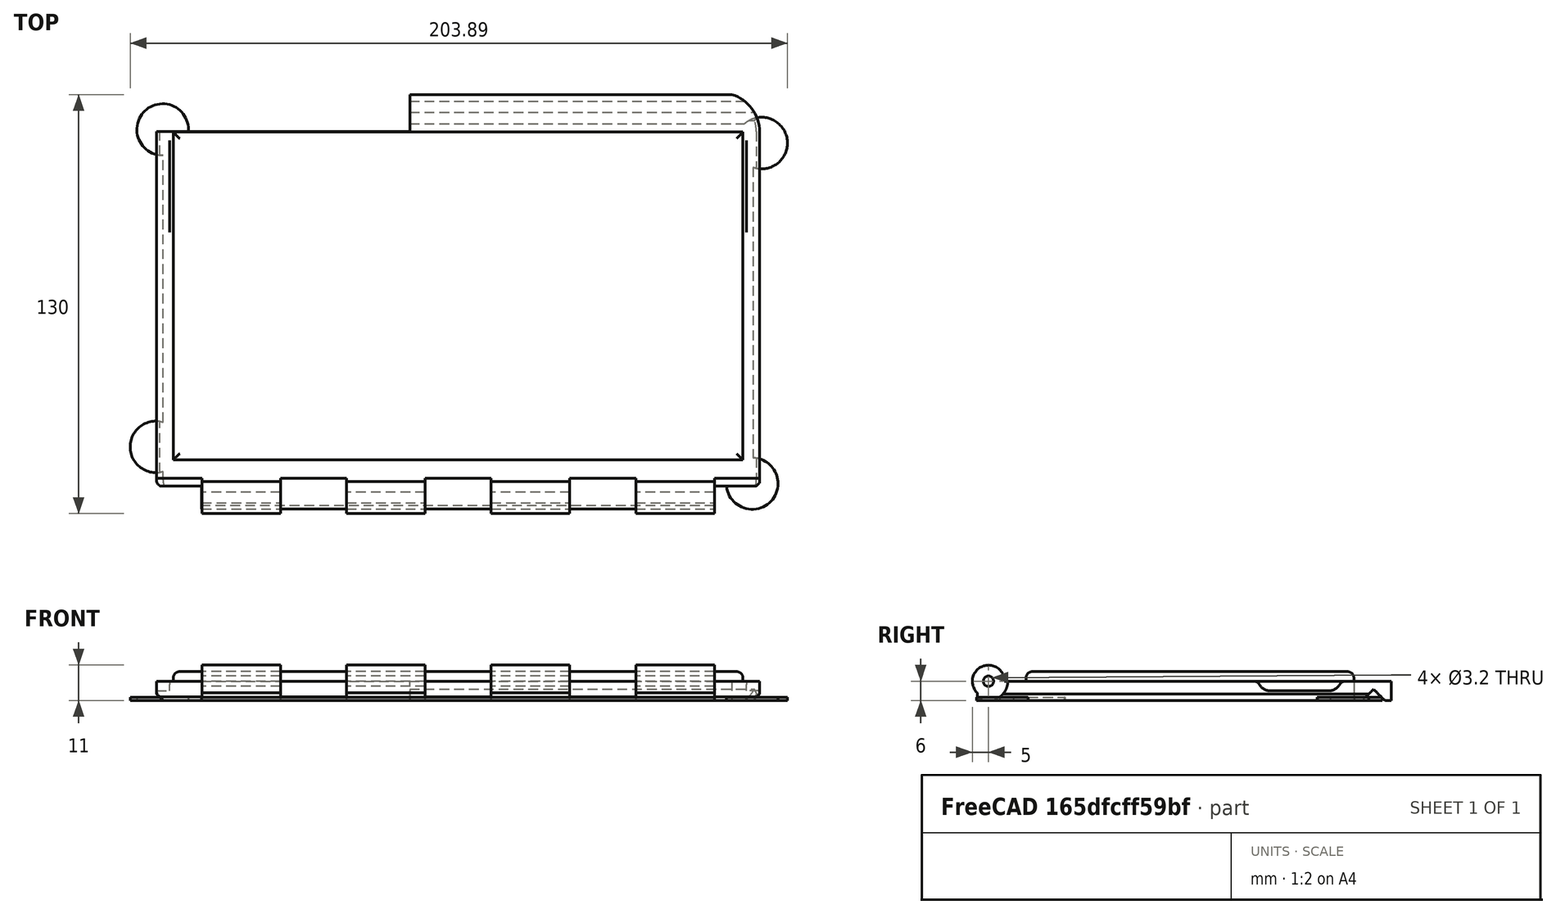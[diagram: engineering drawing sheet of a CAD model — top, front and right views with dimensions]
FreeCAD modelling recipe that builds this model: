
FCSTD DOCUMENT  (FreeCAD 0.19R)
Label: SwitchCaseSmallRLidLatch6mm
License: All rights reserved
LicenseURL: http://en.wikipedia.org/wiki/All_rights_reserved
objects: Sketcher::SketchObject×13, PartDesign::Pocket×8, PartDesign::Pad×4, PartDesign::Chamfer×3, PartDesign::Fillet×2, Mesh::Feature×1, PartDesign::Body×1, PartDesign::LinearPattern×1
note: 49 computed .brp shape members not serialized (recipe doc carries the construction recipe); baked Part::Feature solids carry a one-line shape summary decoded from their .brp

FEATURE [Sketcher::SketchObject] Sketch
  FullyConstrained = false
  MapMode = 5
  Support = -> [XY_Plane]
  sketch-geometry (4):
    g0: LineSegment StartX=-100 StartY=62.5 StartZ=0 EndX=100 EndY=62.5 EndZ=0
    g1: LineSegment StartX=100 StartY=62.5 StartZ=0 EndX=100 EndY=-66 EndZ=0
    g2: LineSegment StartX=100 StartY=-66 StartZ=0 EndX=-100 EndY=-66 EndZ=0
    g3: LineSegment StartX=-100 StartY=-66 StartZ=0 EndX=-100 EndY=62.5 EndZ=0
  constraints (11):
    c: Coincident(g0,g1)
    c: Coincident(g1,g2)
    c: Coincident(g2,g3)
    c: Coincident(g3,g0)
    c: Horizontal(g0)
    c: Horizontal(g2)
    c: Vertical(g1)
    c: Vertical(g3)
    c: Distance(g0) = 200
    c: DistanceY(g2) = -66
    c: DistanceY(g0) = 62.5
FEATURE [PartDesign::Pad] Pad
  Direction = (1,1,1)
  Length = 6
  Length2 = 100
  Profile = -> Sketch
  Type = 0
FEATURE [Sketcher::SketchObject] Sketch001
  FullyConstrained = true
  MapMode = 5
  Placement = pos=(0,0,6) rot=(0,0,1;0rad)
  Support = -> [Pad]
  sketch-geometry (4):
    g0: LineSegment StartX=-88.375 StartY=50.875 StartZ=0 EndX=88.375 EndY=50.875 EndZ=0
    g1: LineSegment StartX=88.375 StartY=50.875 StartZ=0 EndX=88.375 EndY=-50.875 EndZ=0
    g2: LineSegment StartX=88.375 StartY=-50.875 StartZ=0 EndX=-88.375 EndY=-50.875 EndZ=0
    g3: LineSegment StartX=-88.375 StartY=-50.875 StartZ=0 EndX=-88.375 EndY=50.875 EndZ=0
  constraints (11):
    c: Coincident(g0,g1)
    c: Coincident(g1,g2)
    c: Coincident(g2,g3)
    c: Coincident(g3,g0)
    c: Horizontal(g0)
    c: Horizontal(g2)
    c: Vertical(g1)
    c: Vertical(g3)
    c: Distance(g0) = 176.75
    c: Distance(g1) = 101.75
    c: Symmetric(g0,g2,g-1)
FEATURE [PartDesign::Pad] Pad001
  BaseFeature = -> Pad
  Direction = (1,1,1)
  Length = 3
  Length2 = 100
  Profile = -> Sketch001
  Type = 0
FEATURE [Sketcher::SketchObject] Sketch003
  ExternalGeometry = -> [Pad001]
  FullyConstrained = true
  MapMode = 5
  Placement = pos=(0,0,0) rot=(1,0,0;3.14159rad)
  Support = -> [Pad001]
  sketch-geometry (4):
    g0: LineSegment StartX=-15 StartY=-62.5 StartZ=0 EndX=-100 EndY=-62.5 EndZ=0
    g1: LineSegment StartX=-100 StartY=-62.5 StartZ=0 EndX=-100 EndY=-51 EndZ=0
    g2: LineSegment StartX=-100 StartY=-51 StartZ=0 EndX=-15 EndY=-51 EndZ=0
    g3: LineSegment StartX=-15 StartY=-51 StartZ=0 EndX=-15 EndY=-62.5 EndZ=0
  constraints (11):
    c: Coincident(g0,g1)
    c: Coincident(g1,g2)
    c: Coincident(g2,g3)
    c: Coincident(g3,g0)
    c: Horizontal(g0)
    c: Horizontal(g2)
    c: Vertical(g1)
    c: Vertical(g3)
    c: Distance(g1) = 11.5
    c: DistanceX(g0) = -15
    c: Coincident(g0,g-3)
FEATURE [PartDesign::Pocket] Pocket
  BaseFeature = -> Pad001
  Length = 5
  Length2 = 100
  Profile = -> Sketch003
  Type = 1
FEATURE [Sketcher::SketchObject] Sketch005
  FullyConstrained = true
  MapMode = 5
  Placement = pos=(100,0,0) rot=(0.57735,0.57735,0.57735;2.0944rad)
  Support = -> [Pocket]
FEATURE [Sketcher::SketchObject] Sketch006
  ExternalGeometry = -> [Pocket]
  FullyConstrained = true
  MapMode = 5
  Placement = pos=(-15,0,0) rot=(0.57735,-0.57735,-0.57735;2.0944rad)
  Support = -> [Pocket]
  sketch-geometry (4):
    g0: LineSegment StartX=-56.9645 StartY=3.53553 StartZ=0 EndX=-60.5 EndY=0 EndZ=0
    g1: LineSegment StartX=-60.5 StartY=0 StartZ=0 EndX=-56.9645 EndY=-3.53553 EndZ=0
    g2: LineSegment StartX=-56.9645 StartY=-3.53553 StartZ=0 EndX=-53.4289 EndY=0 EndZ=0
    g3: LineSegment StartX=-53.4289 StartY=0 StartZ=0 EndX=-56.9645 EndY=3.53553 EndZ=0
  constraints (12):
    c: Coincident(g0,g1)
    c: Coincident(g1,g2)
    c: Coincident(g2,g3)
    c: Coincident(g3,g0)
    c: Perpendicular(g0,g3)
    c: Perpendicular(g0,g1)
    c: Equal(g3,g0)
    c: Equal(g0,g1)
    c: Distance(g3) = 5
    c: PointOnObject(g0,g-4)
    c: PointOnObject(g2,g-4)
    c: Distance(g0,g-4) = 2
FEATURE [PartDesign::Pocket] Pocket001  label="pocket_dovetail"
  BaseFeature = -> Pocket
  Length = 5
  Length2 = 100
  Profile = -> Sketch006
  Type = 1
FEATURE [Sketcher::SketchObject] Sketch012
  FullyConstrained = true
  MapMode = 5
  Placement = pos=(-93.5,-1.2e-14,0) rot=(0.57735,-0.57735,-0.57735;2.0944rad)
  sketch-geometry (4):
    g0: ArcOfCircle CenterX=-43 CenterY=7 CenterZ=0 NormalX=0 NormalY=0 NormalZ=1 AngleXU=0 Radius=4 StartAngle=1.5708 EndAngle=4.71239
    g1: ArcOfCircle CenterX=-25 CenterY=7 CenterZ=0 NormalX=0 NormalY=0 NormalZ=1 AngleXU=0 Radius=4 StartAngle=4.71239 EndAngle=7.85398
    g2: LineSegment StartX=-43 StartY=3 StartZ=0 EndX=-25 EndY=3 EndZ=0
    g3: LineSegment StartX=-43 StartY=11 StartZ=0 EndX=-25 EndY=11 EndZ=0
  constraints (10):
    c: Tangent(g0,g3) = 1.5708
    c: Tangent(g0,g2) = -1.5708
    c: Tangent(g2,g1) = -1.5708
    c: Tangent(g3,g1) = 1.5708
    c: Horizontal(g2)
    c: Equal(g0,g1)
    c: Distance(g3) = 18
    c: Distance(g1,g1) = 8
    c: DistanceY(g1) = 3
    c: DistanceX(g1) = -25
FEATURE [Sketcher::SketchObject] Sketch013
  FullyConstrained = true
  MapMode = 5
  Placement = pos=(93.5,0,0) rot=(0.57735,0.57735,0.57735;2.0944rad)
  sketch-geometry (4):
    g0: ArcOfCircle CenterX=25 CenterY=7 CenterZ=0 NormalX=0 NormalY=0 NormalZ=1 AngleXU=0 Radius=4 StartAngle=1.5708 EndAngle=4.71239
    g1: ArcOfCircle CenterX=43 CenterY=7 CenterZ=0 NormalX=0 NormalY=0 NormalZ=1 AngleXU=0 Radius=4 StartAngle=4.71239 EndAngle=7.85398
    g2: LineSegment StartX=25 StartY=3 StartZ=0 EndX=43 EndY=3 EndZ=0
    g3: LineSegment StartX=25 StartY=11 StartZ=0 EndX=43 EndY=11 EndZ=0
  constraints (10):
    c: Tangent(g0,g3) = 1.5708
    c: Tangent(g0,g2) = -1.5708
    c: Tangent(g2,g1) = -1.5708
    c: Tangent(g3,g1) = 1.5708
    c: Horizontal(g2)
    c: Equal(g0,g1)
    c: Distance(g1,g1) = 8
    c: Distance(g3) = 18
    c: DistanceY(g0) = 3
    c: DistanceX(g0) = 25
FEATURE [Mesh::Feature] Mesh  label="Pad003 (Meshed)"
FEATURE [PartDesign::Body] Body
  Group = -> [Sketch,Pad,Sketch001,Pad001,Sketch003,Pocket,Sketch005,Sketch006,Pocket001,Sketch007,Sketch008,Pad002,Sketch009,Pocket002,LinearPattern,Sketch010,Pocket003,Chamfer,Sketch011,Pocket004,Pocket005,Chamfer001,Sketch012,Sketch013,Chamfer002,Pocket006,Pocket007,Fillet,Fillet001,Sketch014,Pad003]
  Origin = -> Origin
  Tip = -> Pad003
FEATURE [Sketcher::SketchObject] Sketch007
  FullyConstrained = true
  MapMode = 5
  Placement = pos=(0,0,0) rot=(1,0,0;3.14159rad)
  Support = -> [Pocket004]
  sketch-geometry (9):
    g0: LineSegment StartX=-93.5 StartY=57 StartZ=0 EndX=-93.5 EndY=-51 EndZ=0
    g1: LineSegment StartX=-81.5 StartY=-63 StartZ=0 EndX=81.5 EndY=-63 EndZ=0
    g2: LineSegment StartX=93.5 StartY=-51 StartZ=0 EndX=93.5 EndY=57 EndZ=0
    g3: LineSegment StartX=81.5 StartY=69 StartZ=0 EndX=-81.5 EndY=69 EndZ=0
    g4: ArcOfCircle CenterX=81.5 CenterY=57 CenterZ=0 NormalX=0 NormalY=0 NormalZ=1 AngleXU=0 Radius=12 StartAngle=0 EndAngle=1.5708
    g5: ArcOfCircle CenterX=-81.5 CenterY=57 CenterZ=0 NormalX=0 NormalY=0 NormalZ=1 AngleXU=0 Radius=12 StartAngle=1.5708 EndAngle=3.14159
    g6: ArcOfCircle CenterX=-81.5 CenterY=-51 CenterZ=0 NormalX=0 NormalY=0 NormalZ=1 AngleXU=0 Radius=12 StartAngle=3.14159 EndAngle=4.71239
    g7: ArcOfCircle CenterX=81.5 CenterY=-51 CenterZ=0 NormalX=0 NormalY=0 NormalZ=1 AngleXU=0 Radius=12 StartAngle=4.71239 EndAngle=6.28319
    g8: Circle CenterX=0 CenterY=0 CenterZ=0 NormalX=0 NormalY=0 NormalZ=1 AngleXU=0 Radius=191.08
  constraints (21):
    c: Equal(g2,g0)
    c: Horizontal(g3)
    c: Vertical(g2)
    c: Equal(g1,g3)
    c: Tangent(g3,g4) = -1.5708
    c: Tangent(g2,g4) = -1.5708
    c: Tangent(g3,g5) = -1.5708
    c: Tangent(g0,g5) = -1.5708
    c: Tangent(g0,g6) = -1.5708
    c: Tangent(g1,g6) = -1.5708
    c: Tangent(g1,g7) = -1.5708
    c: Tangent(g2,g7) = -1.5708
    c: Radius(g4) = 12
    c: Equal(g4,g5)
    c: Equal(g4,g6)
    c: Symmetric(g2,g0,g-2)
    c: DistanceY(g3) = 69
    c: DistanceY(g1) = -63
    c: Distance(g2,g0) = 187
    c: Coincident(g8,g-1)
    c: Radius(g8) = 191.08
FEATURE [Sketcher::SketchObject] Sketch008
  ExternalGeometry = -> [Sketch007,Pocket001]
  FullyConstrained = true
  MapMode = 5
  Placement = pos=(100,0,0) rot=(0.57735,0.57735,0.57735;2.0944rad)
  Support = -> [Pocket001]
  sketch-geometry (1):
    g0: Circle CenterX=-62.5 CenterY=6 CenterZ=0 NormalX=0 NormalY=0 NormalZ=1 AngleXU=0 Radius=5
  constraints (3):
    c: Radius(g0) = 5
    c: PointOnObject(g0,g-4)
    c: DistanceX(g0) = -62.5
FEATURE [PartDesign::Pad] Pad002
  BaseFeature = -> Pocket001
  Direction = (1,1,1)
  Length = 200
  Length2 = 100
  Profile = -> Sketch008
  Reversed = true
  Type = 0
FEATURE [Sketcher::SketchObject] Sketch009
  ExternalGeometry = -> [Pad002]
  FullyConstrained = true
  MapMode = 5
  Placement = pos=(100,0,0) rot=(0.57735,0.57735,0.57735;2.0944rad)
  Support = -> [Pad002]
  sketch-geometry (1):
    g0: Circle CenterX=-62.5 CenterY=6 CenterZ=0 NormalX=0 NormalY=0 NormalZ=1 AngleXU=0 Radius=6
  constraints (3):
    c: Radius(g0) = 6
    c: PointOnObject(g0,g-6)
    c: DistanceX(g0) = -62.5
FEATURE [PartDesign::Pocket] Pocket002  label="hingepocket"
  BaseFeature = -> Pad002
  Length = 20.5
  Length2 = 100
  Profile = -> Sketch009
  Type = 0
FEATURE [PartDesign::LinearPattern] LinearPattern
  BaseFeature = -> Pocket002
  Direction = -> X_Axis
  Length = 179.5
  Occurrences = 5
  Originals = -> [Pocket002]
  Reversed = true
FEATURE [Sketcher::SketchObject] Sketch010
  ExternalGeometry = -> [LinearPattern]
  FullyConstrained = true
  MapMode = 5
  Placement = pos=(-79.5,0,0) rot=(0.57735,-0.57735,-0.57735;2.0944rad)
  Support = -> [LinearPattern]
  sketch-geometry (1):
    g0: Circle CenterX=62.5 CenterY=6 CenterZ=0 NormalX=0 NormalY=0 NormalZ=1 AngleXU=0 Radius=1.6
  constraints (3):
    c: Radius(g0) = 1.6
    c: DistanceX(g0) = 62.5
    c: DistanceY(g0) = 6
FEATURE [PartDesign::Pocket] Pocket003  label="hingepin"
  BaseFeature = -> LinearPattern
  Length = 5
  Length2 = 100
  Profile = -> Sketch010
  Type = 1
FEATURE [PartDesign::Chamfer] Chamfer
  Angle = 45
  Base = -> Pocket003 [Edge46]
  BaseFeature = -> Pocket003
  ChamferType = 0
  FlipDirection = false
  Size = 1
  Size2 = 1
  SupportTransform = false
FEATURE [Sketcher::SketchObject] Sketch011
  FullyConstrained = false
  MapMode = 5
  Placement = pos=(0,0,0) rot=(1,0,0;3.14159rad)
  Support = -> [Chamfer]
  sketch-geometry (8):
    g0: LineSegment StartX=-103.879 StartY=59 StartZ=0 EndX=-79.55 EndY=59 EndZ=0
    g1: LineSegment StartX=-79.55 StartY=59 StartZ=0 EndX=-79.55 EndY=72.9041 EndZ=0
    g2: LineSegment StartX=-79.55 StartY=72.9041 StartZ=0 EndX=-103.879 EndY=72.9041 EndZ=0
    g3: LineSegment StartX=-103.879 StartY=72.9041 StartZ=0 EndX=-103.879 EndY=59 EndZ=0
    g4: LineSegment StartX=79.55 StartY=72.9041 StartZ=0 EndX=107.401 EndY=72.9041 EndZ=0
    g5: LineSegment StartX=107.401 StartY=72.9041 StartZ=0 EndX=107.401 EndY=59 EndZ=0
    g6: LineSegment StartX=107.401 StartY=59 StartZ=0 EndX=79.55 EndY=59 EndZ=0
    g7: LineSegment StartX=79.55 StartY=59 StartZ=0 EndX=79.55 EndY=72.9041 EndZ=0
  constraints (20):
    c: Coincident(g0,g1)
    c: Coincident(g1,g2)
    c: Coincident(g2,g3)
    c: Coincident(g3,g0)
    c: Horizontal(g0)
    c: Horizontal(g2)
    c: Vertical(g1)
    c: Vertical(g3)
    c: Coincident(g4,g5)
    c: Coincident(g5,g6)
    c: Coincident(g6,g7)
    c: Coincident(g7,g4)
    c: Horizontal(g4)
    c: Horizontal(g6)
    c: Vertical(g5)
    c: Vertical(g7)
    c: DistanceY(g6) = 59
    c: DistanceY(g0) = 59
    c: Symmetric(g1,g4,g-2)
    c: Distance(g1,g4) = 159.1
FEATURE [PartDesign::Pocket] Pocket004
  BaseFeature = -> Chamfer
  Length = 5
  Length2 = 100
  Profile = -> Sketch011
  Type = 0
FEATURE [PartDesign::Pocket] Pocket005
  BaseFeature = -> Pocket004
  Length = 5
  Length2 = 100
  Profile = -> Sketch007
  Type = 1
FEATURE [PartDesign::Chamfer] Chamfer001
  Angle = 45
  Base = -> Pocket005 [Edge5]
  BaseFeature = -> Pocket005
  ChamferType = 0
  FlipDirection = false
  Size = 2
  Size2 = 1
  SupportTransform = false
FEATURE [PartDesign::Chamfer] Chamfer002
  Angle = 45
  Base = -> Chamfer001 [Edge14]
  BaseFeature = -> Chamfer001
  ChamferType = 0
  FlipDirection = false
  Size = 2
  Size2 = 1
  SupportTransform = false
FEATURE [PartDesign::Pocket] Pocket006
  BaseFeature = -> Chamfer002
  Length = 4
  Length2 = 100
  Profile = -> Sketch013
  Type = 0
FEATURE [PartDesign::Pocket] Pocket007
  BaseFeature = -> Pocket006
  Length = 4
  Length2 = 100
  Profile = -> Sketch012
  Type = 0
FEATURE [PartDesign::Fillet] Fillet
  Base = -> Pocket007 [Edge78,Edge76,Edge70,Edge72]
  BaseFeature = -> Pocket007
  Radius = 2
  SupportTransform = false
FEATURE [PartDesign::Fillet] Fillet001
  Base = -> Fillet [Face66]
  BaseFeature = -> Fillet
  Radius = 2
  SupportTransform = false
FEATURE [Sketcher::SketchObject] Sketch014
  FullyConstrained = false
  MapMode = 5
  Placement = pos=(0,0,0) rot=(1,0,0;3.14159rad)
  Support = -> [Fillet001]
  sketch-geometry (4):
    g0: Circle CenterX=-93.7329 CenterY=46.7924 CenterZ=0 NormalX=0 NormalY=0 NormalZ=1 AngleXU=0 Radius=8
    g1: Circle CenterX=91.242 CenterY=58.1629 CenterZ=0 NormalX=0 NormalY=0 NormalZ=1 AngleXU=0 Radius=8
    g2: Circle CenterX=-91.6615 CenterY=-51.6456 CenterZ=0 NormalX=0 NormalY=0 NormalZ=1 AngleXU=0 Radius=8
    g3: Circle CenterX=94.1626 CenterY=-47.4545 CenterZ=0 NormalX=0 NormalY=0 NormalZ=1 AngleXU=0 Radius=8
  constraints (4):
    c: Radius(g0) = 8
    c: Equal(g0,g2)
    c: Equal(g0,g1)
    c: Equal(g0,g3)
FEATURE [PartDesign::Pad] Pad003
  BaseFeature = -> Fillet001
  Direction = (1,1,1)
  Length = 1
  Length2 = 100
  Profile = -> Sketch014
  Reversed = true
  Type = 0
